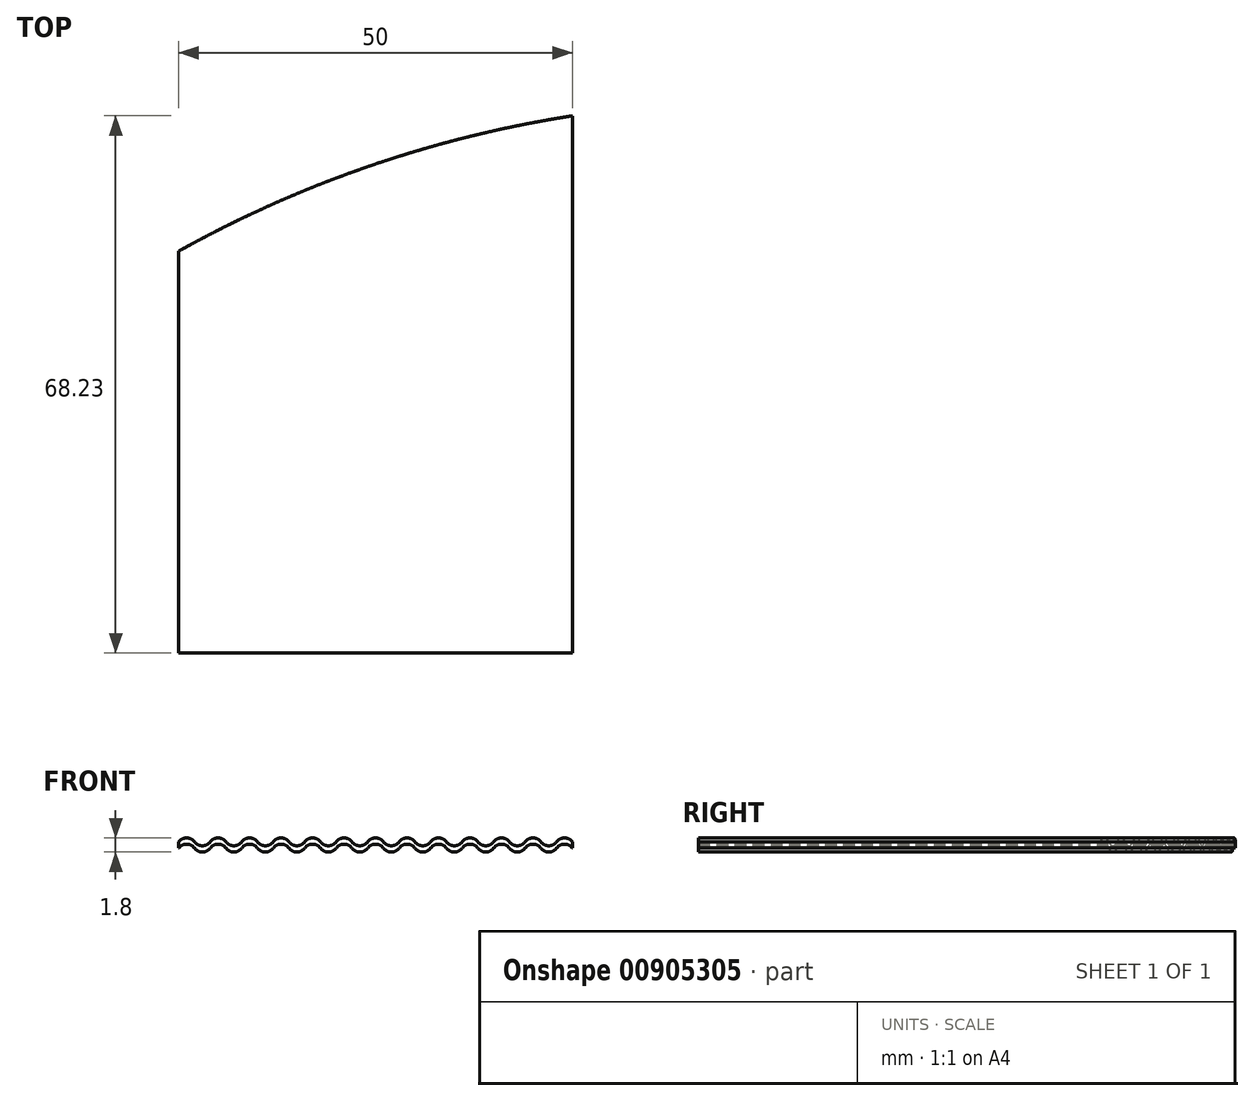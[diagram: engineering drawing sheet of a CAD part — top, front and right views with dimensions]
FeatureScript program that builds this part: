
annotation { "Feature Type Name" : "Feature", "Feature Type Description" : "" }
export const myFeature = defineFeature(function(context is Context, id is Id, definition is map)
    precondition{}
    {
        {
            var Q0;
            Q0=qCreatedBy(makeId("Front.planeOp"),FACE);
            var sketch = newSketch(context, id + "F0", { "sketchPlane" : qUnion([Q0])});
            skArc(sketch, "E0", {"start": v(-19, -0.4) * mm, "mid": v(-20, 0.1) * mm, "end": v(-21, -0.4) * mm});
            skArc(sketch, "E1", {"start": v(-23, -0.4) * mm, "mid": v(-22, -0.9) * mm, "end": v(-21, -0.4) * mm});
            skArc(sketch, "E2", {"start": v(-23, -0.4) * mm, "mid": v(-24, 0.1) * mm, "end": v(-25, -0.4) * mm});
            skArc(sketch, "E3", {"start": v(5, -0.4) * mm, "mid": v(6, -0.9) * mm, "end": v(7, -0.4) * mm});
            skArc(sketch, "E4", {"start": v(9, -0.4) * mm, "mid": v(8, 0.1) * mm, "end": v(7, -0.4) * mm});
            skArc(sketch, "E5", {"start": v(9, -0.4) * mm, "mid": v(10, -0.9) * mm, "end": v(11, -0.4) * mm});
            skArc(sketch, "E6", {"start": v(13, -0.4) * mm, "mid": v(12, 0.1) * mm, "end": v(11, -0.4) * mm});
            skArc(sketch, "E7", {"start": v(13, -0.4) * mm, "mid": v(14, -0.9) * mm, "end": v(15, -0.4) * mm});
            skArc(sketch, "E8", {"start": v(17, -0.4) * mm, "mid": v(16, 0.1) * mm, "end": v(15, -0.4) * mm});
            skArc(sketch, "E9", {"start": v(25, -0.4) * mm, "mid": v(24, 0.1) * mm, "end": v(23, -0.4) * mm});
            skArc(sketch, "E10", {"start": v(21, -0.4) * mm, "mid": v(22, -0.9) * mm, "end": v(23, -0.4) * mm});
            skArc(sketch, "E11", {"start": v(21, -0.4) * mm, "mid": v(20, 0.1) * mm, "end": v(19, -0.4) * mm});
            skArc(sketch, "E12", {"start": v(17, -0.4) * mm, "mid": v(18, -0.9) * mm, "end": v(19, -0.4) * mm});
            skArc(sketch, "E13", {"start": v(5, -0.4) * mm, "mid": v(4, 0.1) * mm, "end": v(3, -0.4) * mm});
            skArc(sketch, "E14", {"start": v(1, -0.4) * mm, "mid": v(2, -0.9) * mm, "end": v(3, -0.4) * mm});
            skArc(sketch, "E15", {"start": v(1, -0.4) * mm, "mid": v(0, 0.1) * mm, "end": v(-1, -0.4) * mm});
            skArc(sketch, "E16", {"start": v(-3, -0.4) * mm, "mid": v(-2, -0.9) * mm, "end": v(-1, -0.4) * mm});
            skArc(sketch, "E17", {"start": v(-3, -0.4) * mm, "mid": v(-4, 0.1) * mm, "end": v(-5, -0.4) * mm});
            skArc(sketch, "E18", {"start": v(-7, -0.4) * mm, "mid": v(-6, -0.9) * mm, "end": v(-5, -0.4) * mm});
            skArc(sketch, "E19", {"start": v(-7, -0.4) * mm, "mid": v(-8, 0.1) * mm, "end": v(-9, -0.4) * mm});
            skArc(sketch, "E20", {"start": v(-11, -0.4) * mm, "mid": v(-10, -0.9) * mm, "end": v(-9, -0.4) * mm});
            skArc(sketch, "E21", {"start": v(-11, -0.4) * mm, "mid": v(-12, 0.1) * mm, "end": v(-13, -0.4) * mm});
            skArc(sketch, "E22", {"start": v(-15, -0.4) * mm, "mid": v(-14, -0.9) * mm, "end": v(-13, -0.4) * mm});
            skArc(sketch, "E23", {"start": v(-15, -0.4) * mm, "mid": v(-16, 0.1) * mm, "end": v(-17, -0.4) * mm});
            skArc(sketch, "E24", {"start": v(-19, -0.4) * mm, "mid": v(-18, -0.9) * mm, "end": v(-17, -0.4) * mm});
            skArc(sketch, "E25", {"start": v(-19, 0.4) * mm, "mid": v(-20, 0.9) * mm, "end": v(-21, 0.4) * mm});
            skArc(sketch, "E26", {"start": v(-23, 0.4) * mm, "mid": v(-22, -0.1) * mm, "end": v(-21, 0.4) * mm});
            skArc(sketch, "E27", {"start": v(-23, 0.4) * mm, "mid": v(-24, 0.9) * mm, "end": v(-25, 0.4) * mm});
            skArc(sketch, "E28", {"start": v(5, 0.4) * mm, "mid": v(6, -0.1) * mm, "end": v(7, 0.4) * mm});
            skArc(sketch, "E29", {"start": v(9, 0.4) * mm, "mid": v(8, 0.9) * mm, "end": v(7, 0.4) * mm});
            skArc(sketch, "E30", {"start": v(9, 0.4) * mm, "mid": v(10, -0.1) * mm, "end": v(11, 0.4) * mm});
            skArc(sketch, "E31", {"start": v(13, 0.4) * mm, "mid": v(12, 0.9) * mm, "end": v(11, 0.4) * mm});
            skArc(sketch, "E32", {"start": v(13, 0.4) * mm, "mid": v(14, -0.1) * mm, "end": v(15, 0.4) * mm});
            skArc(sketch, "E33", {"start": v(17, 0.4) * mm, "mid": v(16, 0.9) * mm, "end": v(15, 0.4) * mm});
            skArc(sketch, "E34", {"start": v(25, 0.4) * mm, "mid": v(24, 0.9) * mm, "end": v(23, 0.4) * mm});
            skArc(sketch, "E35", {"start": v(21, 0.4) * mm, "mid": v(22, -0.1) * mm, "end": v(23, 0.4) * mm});
            skArc(sketch, "E36", {"start": v(21, 0.4) * mm, "mid": v(20, 0.9) * mm, "end": v(19, 0.4) * mm});
            skArc(sketch, "E37", {"start": v(17, 0.4) * mm, "mid": v(18, -0.1) * mm, "end": v(19, 0.4) * mm});
            skArc(sketch, "E38", {"start": v(5, 0.4) * mm, "mid": v(4, 0.9) * mm, "end": v(3, 0.4) * mm});
            skArc(sketch, "E39", {"start": v(1, 0.4) * mm, "mid": v(2, -0.1) * mm, "end": v(3, 0.4) * mm});
            skArc(sketch, "E40", {"start": v(1, 0.4) * mm, "mid": v(0, 0.9) * mm, "end": v(-1, 0.4) * mm});
            skArc(sketch, "E41", {"start": v(-3, 0.4) * mm, "mid": v(-2, -0.1) * mm, "end": v(-1, 0.4) * mm});
            skArc(sketch, "E42", {"start": v(-3, 0.4) * mm, "mid": v(-4, 0.9) * mm, "end": v(-5, 0.4) * mm});
            skArc(sketch, "E43", {"start": v(-7, 0.4) * mm, "mid": v(-6, -0.1) * mm, "end": v(-5, 0.4) * mm});
            skArc(sketch, "E44", {"start": v(-7, 0.4) * mm, "mid": v(-8, 0.9) * mm, "end": v(-9, 0.4) * mm});
            skArc(sketch, "E45", {"start": v(-11, 0.4) * mm, "mid": v(-10, -0.1) * mm, "end": v(-9, 0.4) * mm});
            skArc(sketch, "E46", {"start": v(-11, 0.4) * mm, "mid": v(-12, 0.9) * mm, "end": v(-13, 0.4) * mm});
            skArc(sketch, "E47", {"start": v(-15, 0.4) * mm, "mid": v(-14, -0.1) * mm, "end": v(-13, 0.4) * mm});
            skArc(sketch, "E48", {"start": v(-15, 0.4) * mm, "mid": v(-16, 0.9) * mm, "end": v(-17, 0.4) * mm});
            skArc(sketch, "E49", {"start": v(-19, 0.4) * mm, "mid": v(-18, -0.1) * mm, "end": v(-17, 0.4) * mm});
            skLineSegment(sketch, "E50", {"start": v(-25, 0.4) * mm, "end": v(-25, -0.4) * mm});
            skLineSegment(sketch, "E51", {"start": v(25, 0.4) * mm, "end": v(25, -0.4) * mm});
            skSolve(sketch);
        }
        {
            var Q0;
            Q0=qSketchRegion(id+"F0",true);
            extrude(context, id + "F1", {"entities" : qUnion([Q0]), "depth" : 70 * mm, "offsetDistance" : 25 * mm});
        }
        {
            var Q0;
            Q0=qCreatedBy(makeId("Top.planeOp"),FACE);
            var sketch = newSketch(context, id + "F2", { "sketchPlane" : qUnion([Q0])});
            skLineSegment(sketch, "E52", {"start": v(0, 0) * mm, "end": v(0, -150) * mm, "construction": true});
            skCircle(sketch, "E53", {"center": v(48, -150) * mm, "radius": 150 * mm});
            skSolve(sketch);
        }
        {
            var Q0;
            Q0=makeQuery(id+"F2.imprint","IMPRINT",FACE,{"disambiguationData":[TD([[makeQuery(id+"F2.imprint","IMPRINT",EDGE,{"derivedFrom":sQuery(id+"F2.wireOp",EDGE,"E53")}),1.0]])]});
            extrude(context, id + "F3", {"entities" : qUnion([Q0]), "operationType" : NewBodyOperationType.INTERSECT, "depth" : 25 * mm, "offsetDistance" : 25 * mm, "hasSecondDirection" : true, "secondDirectionOppositeDirection" : true, "secondDirectionDepth" : 25 * mm});
        }
    });
